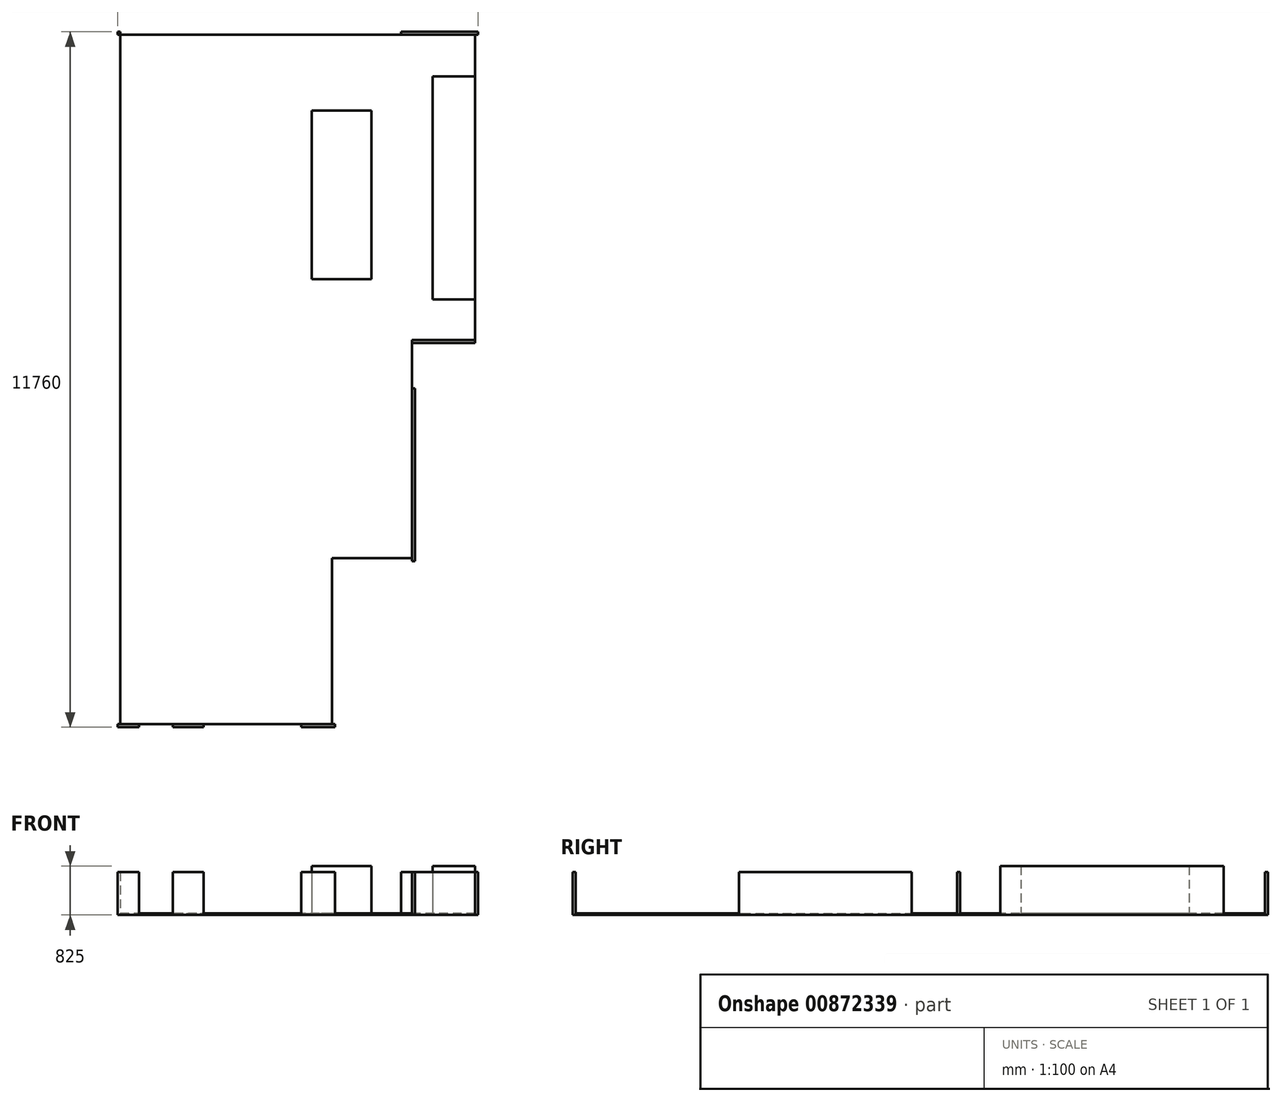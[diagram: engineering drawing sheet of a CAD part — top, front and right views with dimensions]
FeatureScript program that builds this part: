
annotation { "Feature Type Name" : "Feature", "Feature Type Description" : "" }
export const myFeature = defineFeature(function(context is Context, id is Id, definition is map)
    precondition{}
    {
        {
            var Q0;
            Q0=qCreatedBy(makeId("Top.planeOp"),FACE);
            var sketch = newSketch(context, id + "F0", { "sketchPlane" : qUnion([Q0])});
            skLineSegment(sketch, "E0.right", {"start": v(0, 0) * mm, "end": v(0, 11660) * mm});
            skLineSegment(sketch, "E1", {"start": v(0, 0) * mm, "end": v(3580, 0) * mm});
            skLineSegment(sketch, "E2", {"start": v(3580, 0) * mm, "end": v(3580, 2810) * mm});
            skLineSegment(sketch, "E3", {"start": v(3580, 2810) * mm, "end": v(4930, 2810) * mm});
            skLineSegment(sketch, "E4", {"start": v(4930, 2810) * mm, "end": v(4930, 6500) * mm});
            skLineSegment(sketch, "E5", {"start": v(4930, 6500) * mm, "end": v(6000, 6500) * mm});
            skLineSegment(sketch, "E6", {"start": v(6000, 6500) * mm, "end": v(6000, 11660) * mm});
            skLineSegment(sketch, "E7", {"start": v(6000, 11660) * mm, "end": v(0, 11660) * mm});
            skLineSegment(sketch, "E8.bottom", {"start": v(6000, 10959.96) * mm, "end": v(5283.42, 10959.96) * mm});
            skLineSegment(sketch, "E8.top", {"start": v(6000, 7182.64) * mm, "end": v(5283.42, 7182.64) * mm});
            skLineSegment(sketch, "E8.left", {"start": v(6000, 10959.96) * mm, "end": v(6000, 7182.64) * mm});
            skLineSegment(sketch, "E8.right", {"start": v(5283.42, 10959.96) * mm, "end": v(5283.42, 7182.64) * mm});
            skLineSegment(sketch, "E9.bottom", {"start": v(4243.29, 10376.03) * mm, "end": v(3235.6, 10376.03) * mm});
            skLineSegment(sketch, "E9.top", {"start": v(4243.29, 7529.35) * mm, "end": v(3235.6, 7529.35) * mm});
            skLineSegment(sketch, "E9.left", {"start": v(4243.29, 10376.03) * mm, "end": v(4243.29, 7529.35) * mm});
            skLineSegment(sketch, "E9.right", {"start": v(3235.6, 10376.03) * mm, "end": v(3235.6, 7529.35) * mm});
            skLineSegment(sketch, "E10.bottom", {"start": v(-50, 11660) * mm, "end": v(680.75, 11660) * mm});
            skLineSegment(sketch, "E10.top", {"start": v(-50, 11710) * mm, "end": v(680.75, 11710) * mm});
            skLineSegment(sketch, "E10.left", {"start": v(-50, 11660) * mm, "end": v(-50, 11710) * mm});
            skLineSegment(sketch, "E10.right", {"start": v(680.75, 11660) * mm, "end": v(680.75, 11710) * mm});
            skLineSegment(sketch, "E11.bottom", {"start": v(2448.5, 11660) * mm, "end": v(3829.15, 11660) * mm});
            skLineSegment(sketch, "E11.top", {"start": v(2448.5, 11710) * mm, "end": v(3829.15, 11710) * mm});
            skLineSegment(sketch, "E11.left", {"start": v(2448.5, 11660) * mm, "end": v(2448.5, 11710) * mm});
            skLineSegment(sketch, "E11.right", {"start": v(3829.15, 11660) * mm, "end": v(3829.15, 11710) * mm});
            skLineSegment(sketch, "E12.bottom", {"start": v(4745.28, 11660) * mm, "end": v(6050, 11660) * mm});
            skLineSegment(sketch, "E12.top", {"start": v(4745.28, 11710) * mm, "end": v(6050, 11710) * mm});
            skLineSegment(sketch, "E12.left", {"start": v(4745.28, 11660) * mm, "end": v(4745.28, 11710) * mm});
            skLineSegment(sketch, "E12.right", {"start": v(6050, 11660) * mm, "end": v(6050, 11710) * mm});
            skLineSegment(sketch, "E13.bottom", {"start": v(-50, 11660) * mm, "end": v(0, 11660) * mm});
            skLineSegment(sketch, "E13.top", {"start": v(-50, 0) * mm, "end": v(0, 0) * mm});
            skLineSegment(sketch, "E13.left", {"start": v(-50, 11660) * mm, "end": v(-50, 0) * mm});
            skLineSegment(sketch, "E13.right", {"start": v(0, 11660) * mm, "end": v(0, 0) * mm});
            skLineSegment(sketch, "E14", {"start": v(0, 11660) * mm, "end": v(0, 11710) * mm});
            skLineSegment(sketch, "E15", {"start": v(4930, 6450) * mm, "end": v(4159.75, 6450) * mm});
            skLineSegment(sketch, "E16.bottom", {"start": v(6050, 11660) * mm, "end": v(6000, 11660) * mm});
            skLineSegment(sketch, "E16.top", {"start": v(6050, 6450) * mm, "end": v(6000, 6450) * mm});
            skLineSegment(sketch, "E16.left", {"start": v(6050, 11660) * mm, "end": v(6050, 6450) * mm});
            skLineSegment(sketch, "E16.right", {"start": v(6000, 11660) * mm, "end": v(6000, 6450) * mm});
            skLineSegment(sketch, "E17.bottom", {"start": v(6000, 6450) * mm, "end": v(4930, 6450) * mm});
            skLineSegment(sketch, "E17.top", {"start": v(6000, 6500) * mm, "end": v(5082.5, 6500) * mm});
            skLineSegment(sketch, "E17.left", {"start": v(6000, 6450) * mm, "end": v(6000, 6500) * mm});
            skArc(sketch, "E18", {"start": v(4159.75, 6450) * mm, "mid": v(4385.35, 5905.35) * mm, "end": v(4930, 5679.75) * mm, "construction": true});
            skLineSegment(sketch, "E19.bottom", {"start": v(4930, 5679.75) * mm, "end": v(4980, 5679.75) * mm});
            skLineSegment(sketch, "E19.top", {"start": v(4930, 2760) * mm, "end": v(4980, 2760) * mm});
            skLineSegment(sketch, "E19.left", {"start": v(4930, 5679.75) * mm, "end": v(4930, 2760) * mm});
            skLineSegment(sketch, "E19.right", {"start": v(4980, 5679.75) * mm, "end": v(4980, 2760) * mm});
            skLineSegment(sketch, "E20.bottom", {"start": v(-50, 0) * mm, "end": v(3630, 0) * mm});
            skLineSegment(sketch, "E20.top", {"start": v(-50, -50) * mm, "end": v(315.77, -50) * mm});
            skLineSegment(sketch, "E20.left", {"start": v(-50, 0) * mm, "end": v(-50, -50) * mm});
            skLineSegment(sketch, "E20.right", {"start": v(3630, 0) * mm, "end": v(3630, -50) * mm});
            skLineSegment(sketch, "E21.bottom", {"start": v(3630, 0) * mm, "end": v(3580, 0) * mm});
            skLineSegment(sketch, "E21.top", {"start": v(3630, 2810) * mm, "end": v(3580, 2810) * mm});
            skLineSegment(sketch, "E21.left", {"start": v(3630, 0) * mm, "end": v(3630, 2810) * mm});
            skLineSegment(sketch, "E22.bottom", {"start": v(3630, 2810) * mm, "end": v(3680, 2810) * mm});
            skLineSegment(sketch, "E22.top", {"start": v(3630, 2760) * mm, "end": v(3680, 2760) * mm});
            skLineSegment(sketch, "E22.left", {"start": v(3630, 2810) * mm, "end": v(3630, 2760) * mm});
            skLineSegment(sketch, "E22.right", {"start": v(3680, 2810) * mm, "end": v(3680, 2760) * mm});
            skLineSegment(sketch, "E23.left", {"start": v(315.77, 0) * mm, "end": v(315.77, -50) * mm});
            skLineSegment(sketch, "E24.right", {"start": v(3058.62, 0) * mm, "end": v(3058.62, -50) * mm});
            skLineSegment(sketch, "E25", {"start": v(3058.62, -50) * mm, "end": v(3630, -50) * mm});
            skLineSegment(sketch, "E26", {"start": v(884.39, -50) * mm, "end": v(1409.94, -50) * mm});
            skLineSegment(sketch, "E27", {"start": v(884.39, -50) * mm, "end": v(884.39, 0) * mm});
            skLineSegment(sketch, "E28", {"start": v(1409.94, -50) * mm, "end": v(1409.94, 0) * mm});
            skSolve(sketch);
        }
        {
            var Q0;
            {var subQ6=sQuery(id+"F0.wireOp",EDGE,"E3");Q0=makeQuery(id+"F0.imprint","IMPRINT",FACE,{"disambiguationData":[TD([[makeQuery(id+"F0.imprint","IMPRINT",EDGE,{"derivedFrom":subQ6}),1.0]])]});}
            extrude(context, id + "F1", {"entities" : qUnion([Q0]), "oppositeDirection" : true, "depth" : 25 * mm, "offsetDistance" : 25 * mm});
        }
        {
            var Q0;
            Q0=makeQuery(id+"F0.imprint","IMPRINT",FACE,{"disambiguationData":[TD([[makeQuery(id+"F0.imprint","IMPRINT",EDGE,{"derivedFrom":sQuery(id+"F0.wireOp",EDGE,"E20.right")}),-1.0]])]});
            var Q1;
            Q1=makeQuery(id+"F0.imprint","IMPRINT",FACE,{"disambiguationData":[TD([[makeQuery(id+"F0.imprint","IMPRINT",EDGE,{"derivedFrom":sQuery(id+"F0.wireOp",EDGE,"E21.bottom")}),-1.0]])]});
            var Q2;
            Q2=makeQuery(id+"F0.imprint","IMPRINT",FACE,{"disambiguationData":[TD([[makeQuery(id+"F0.imprint","IMPRINT",EDGE,{"derivedFrom":sQuery(id+"F0.wireOp",EDGE,"E22.bottom")}),-1.0]])]});
            var Q3;
            {var subQ3=sQuery(id+"F0.wireOp",EDGE,"E19.bottom");Q3=makeQuery(id+"F0.imprint","IMPRINT",FACE,{"disambiguationData":[TD([[makeQuery(id+"F0.imprint","IMPRINT",EDGE,{"derivedFrom":subQ3}),-1.0]])]});}
            var Q4;
            {var subQ1=sQuery(id+"F0.wireOp",EDGE,"E5");Q4=makeQuery(id+"F0.imprint","IMPRINT",FACE,{"disambiguationData":[TD([[makeQuery(id+"F0.imprint","IMPRINT",EDGE,{"derivedFrom":subQ1}),-1.0]])]});}
            var Q5;
            {var subQ2=sQuery(id+"F0.wireOp",EDGE,"E16.bottom");Q5=makeQuery(id+"F0.imprint","IMPRINT",FACE,{"disambiguationData":[TD([[makeQuery(id+"F0.imprint","IMPRINT",EDGE,{"derivedFrom":subQ2}),1.0]])]});}
            var Q6;
            Q6=makeQuery(id+"F0.imprint","IMPRINT",FACE,{"disambiguationData":[TD([[makeQuery(id+"F0.imprint","IMPRINT",EDGE,{"derivedFrom":sQuery(id+"F0.wireOp",EDGE,"E12.bottom")}),1.0]])]});
            var Q7;
            Q7=makeQuery(id+"F0.imprint","IMPRINT",FACE,{"disambiguationData":[TD([[makeQuery(id+"F0.imprint","IMPRINT",EDGE,{"derivedFrom":sQuery(id+"F0.wireOp",EDGE,"E11.bottom")}),1.0]])]});
            var Q8;
            Q8=makeQuery(id+"F0.imprint","IMPRINT",FACE,{"disambiguationData":[TD([[makeQuery(id+"F0.imprint","IMPRINT",EDGE,{"derivedFrom":sQuery(id+"F0.wireOp",EDGE,"E10.bottom")}),1.0]])]});
            var Q9;
            Q9=makeQuery(id+"F0.imprint","IMPRINT",FACE,{"disambiguationData":[TD([[makeQuery(id+"F0.imprint","IMPRINT",EDGE,{"derivedFrom":sQuery(id+"F0.wireOp",EDGE,"E13.bottom")}),-1.0]])]});
            var Q10;
            {var subQ0=sQuery(id+"F0.wireOp",EDGE,"E10.left");Q10=makeQuery(id+"F0.imprint","IMPRINT",FACE,{"disambiguationData":[TD([[makeQuery(id+"F0.imprint","IMPRINT",EDGE,{"derivedFrom":subQ0}),-1.0]])]});}
            var Q11;
            Q11=makeQuery(id+"F0.imprint","IMPRINT",FACE,{"disambiguationData":[TD([[makeQuery(id+"F0.imprint","IMPRINT",EDGE,{"derivedFrom":sQuery(id+"F0.wireOp",EDGE,"E20.top")}),1.0]])]});
            var Q12;
            Q12=makeQuery(id+"F0.imprint","IMPRINT",FACE,{"disambiguationData":[TD([[makeQuery(id+"F0.imprint","IMPRINT",EDGE,{"derivedFrom":sQuery(id+"F0.wireOp",EDGE,"E26")}),1.0]])]});
            extrude(context, id + "F2", {"entities" : qUnion([Q0, Q1, Q2, Q3, Q4, Q5, Q6, Q7, Q8, Q9, Q10, Q11, Q12]), "operationType" : NewBodyOperationType.ADD, "depth" : 700 * mm, "offsetDistance" : 25 * mm, "hasSecondDirection" : true, "secondDirectionOppositeDirection" : true, "secondDirectionDepth" : 25 * mm});
        }
        {
            var Q0;
            Q0=makeQuery(id+"F0.imprint","IMPRINT",FACE,{"disambiguationData":[TD([[makeQuery(id+"F0.imprint","IMPRINT",EDGE,{"derivedFrom":sQuery(id+"F0.wireOp",EDGE,"E9.bottom")}),1.0]])]});
            var Q1;
            {var subQ0=sQuery(id+"F0.wireOp",EDGE,"E8.bottom");Q1=makeQuery(id+"F0.imprint","IMPRINT",FACE,{"disambiguationData":[TD([[makeQuery(id+"F0.imprint","IMPRINT",EDGE,{"derivedFrom":subQ0}),1.0]])]});}
            extrude(context, id + "F3", {"entities" : qUnion([Q0, Q1]), "operationType" : NewBodyOperationType.ADD, "depth" : 800 * mm, "offsetDistance" : 25 * mm, "hasSecondDirection" : true, "secondDirectionOppositeDirection" : true, "secondDirectionDepth" : 25 * mm});
        }
    });
